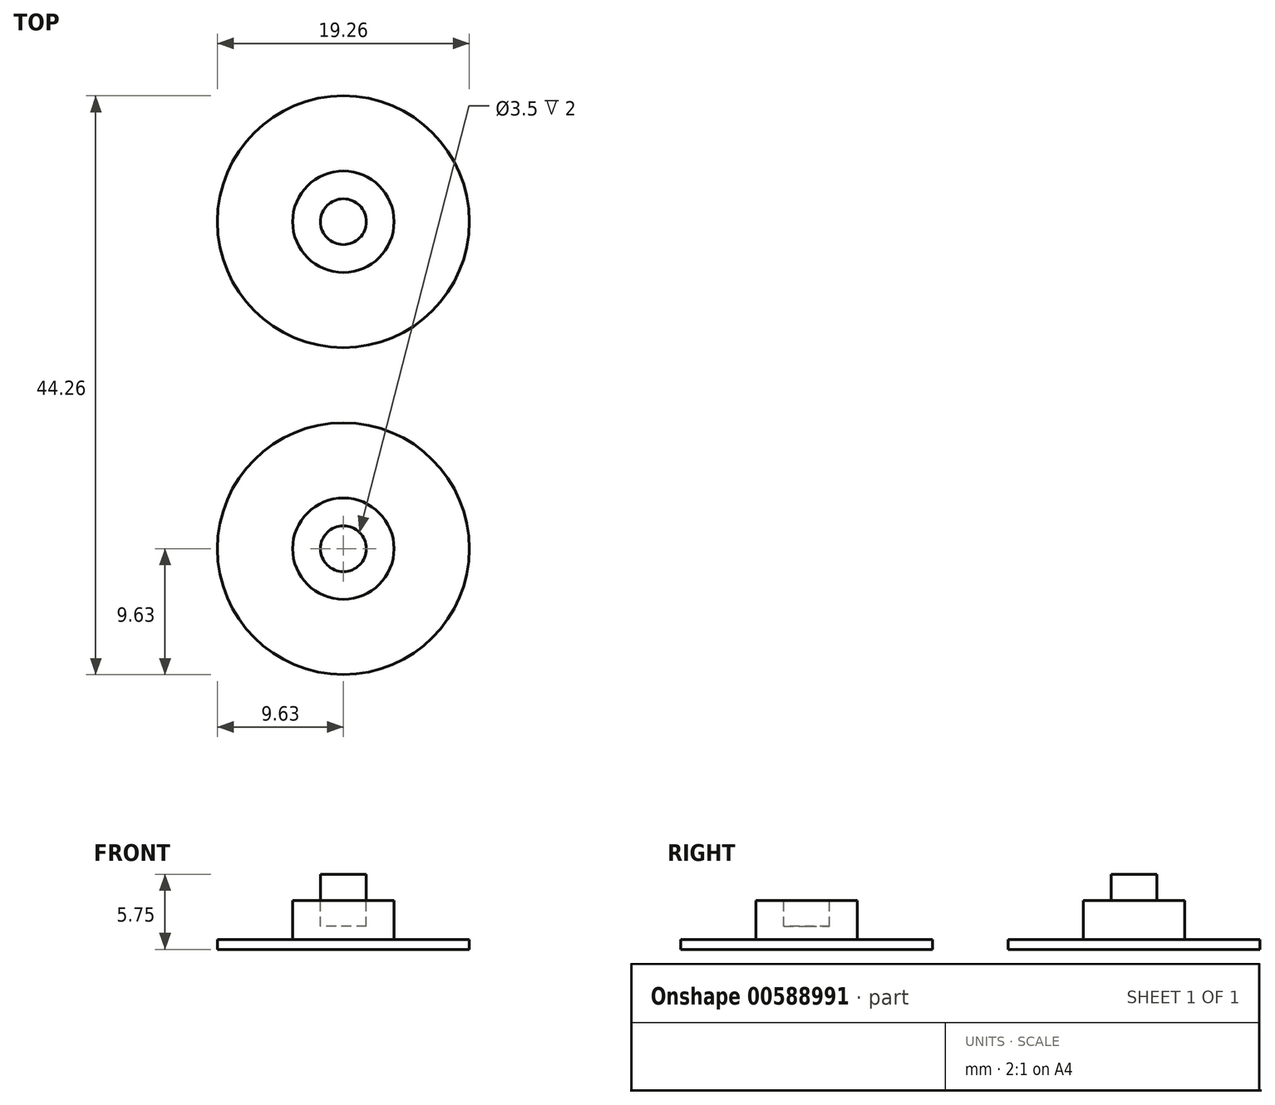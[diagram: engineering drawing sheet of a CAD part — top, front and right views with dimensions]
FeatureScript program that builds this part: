
annotation { "Feature Type Name" : "Feature", "Feature Type Description" : "" }
export const myFeature = defineFeature(function(context is Context, id is Id, definition is map)
    precondition{}
    {
        {
            var Q0;
            Q0=qCreatedBy(makeId("Top.planeOp"),FACE);
            var sketch = newSketch(context, id + "F0", { "sketchPlane" : qUnion([Q0])});
            skCircle(sketch, "E0", {"center": v(0, 0) * mm, "radius": 9.62 * mm});
            skCircle(sketch, "E1", {"center": v(0, 0) * mm, "radius": 3.88 * mm});
            skSolve(sketch);
        }
        {
            var Q0;
            Q0=makeQuery(id+"F0.imprint","IMPRINT",FACE,{"disambiguationData":[TD([[makeQuery(id+"F0.imprint","IMPRINT",EDGE,{"derivedFrom":sQuery(id+"F0.wireOp",EDGE,"E0")}),1.0]])]});
            extrude(context, id + "F1", {"entities" : qUnion([Q0]), "depth" : .75 * mm, "offsetDistance" : 25 * mm});
        }
        {
            var Q0;
            Q0=makeQuery(id+"F0.imprint","IMPRINT",FACE,{"disambiguationData":[TD([[makeQuery(id+"F0.imprint","IMPRINT",EDGE,{"derivedFrom":sQuery(id+"F0.wireOp",EDGE,"E1")}),1.0]])]});
            extrude(context, id + "F2", {"entities" : qUnion([Q0]), "operationType" : NewBodyOperationType.ADD, "depth" : (7.5 / 2) * mm, "offsetDistance" : 25 * mm});
        }
        {
            var Q0;
            Q0=makeQuery(id+"F1.opExtrude","SWEPT_BODY",BODY,{"disambiguationData":[OSD([sQuery(id+"F0.wireOp",EDGE,"E0"),sQuery(id+"F0.wireOp",EDGE,"E1")])]});
            transform(context, id + "F3", {"entities" : qUnion([Q0]), "transformType" : TransformType.TRANSLATION_3D, "dx" : 0 * mm, "dy" : 25 * mm, "dz" : 0 * mm, "makeCopy" : true});
        }
        {
            var Q0;
            Q0=makeQuery(id+"F3.opPattern","COPY",FACE,{"derivedFrom":makeQuery(id+"F2.opExtrude","CAP_FACE",FACE,{"disambiguationData":[OSD([sQuery(id+"F0.wireOp",EDGE,"E1")])],"isStart":false}),"instanceName":"1"});
            var sketch = newSketch(context, id + "F4", { "sketchPlane" : qUnion([Q0])});
            skCircle(sketch, "E2", {"center": v(0, 25) * mm, "radius": 1.75 * mm});
            skCircle(sketch, "E3", {"center": v(0, 0) * mm, "radius": 1.75 * mm});
            skSolve(sketch);
        }
        {
            var Q0;
            Q0=makeQuery(id+"F4.imprint","IMPRINT",FACE,{"disambiguationData":[TD([[makeQuery(id+"F4.imprint","IMPRINT",EDGE,{"derivedFrom":sQuery(id+"F4.wireOp",EDGE,"E2")}),1.0]])]});
            extrude(context, id + "F5", {"entities" : qUnion([Q0]), "operationType" : NewBodyOperationType.ADD, "depth" : 2 * mm, "offsetDistance" : 25 * mm});
        }
        {
            var Q0;
            Q0=makeQuery(id+"F4.imprint","IMPRINT",FACE,{"disambiguationData":[TD([[makeQuery(id+"F4.imprint","IMPRINT",EDGE,{"derivedFrom":sQuery(id+"F4.wireOp",EDGE,"E3")}),1.0]])]});
            extrude(context, id + "F6", {"entities" : qUnion([Q0]), "operationType" : NewBodyOperationType.REMOVE, "oppositeDirection" : true, "depth" : 2 * mm, "offsetDistance" : 25 * mm});
        }
    });
